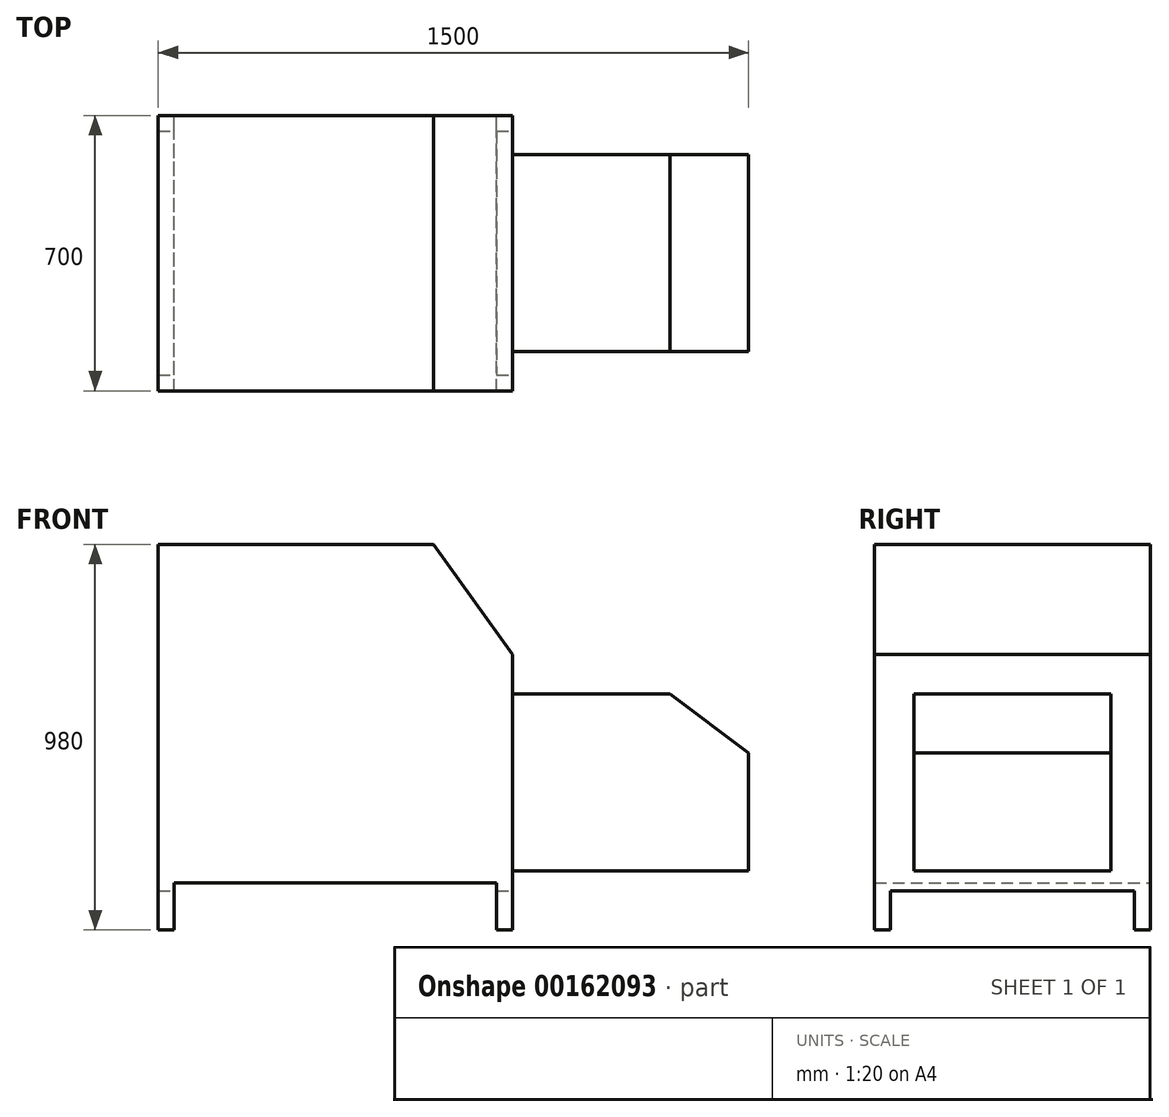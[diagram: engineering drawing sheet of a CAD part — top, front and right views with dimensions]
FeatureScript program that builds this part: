
annotation { "Feature Type Name" : "Feature", "Feature Type Description" : "" }
export const myFeature = defineFeature(function(context is Context, id is Id, definition is map)
    precondition{}
    {
        {
            var Q0;
            Q0=qCreatedBy(makeId("Front.planeOp"),FACE);
            var sketch = newSketch(context, id + "F0", { "sketchPlane" : qUnion([Q0])});
            skLineSegment(sketch, "E0", {"start": v(0, 0) * mm, "end": v(0, 980) * mm});
            skLineSegment(sketch, "E1", {"start": v(0, 980) * mm, "end": v(700, 980) * mm});
            skLineSegment(sketch, "E2", {"start": v(700, 980) * mm, "end": v(900, 700) * mm});
            skLineSegment(sketch, "E3", {"start": v(900, 700) * mm, "end": v(900, 0) * mm});
            skLineSegment(sketch, "E4", {"start": v(900, 0) * mm, "end": v(860, 0) * mm});
            skLineSegment(sketch, "E5", {"start": v(860, 0) * mm, "end": v(860, 120) * mm});
            skLineSegment(sketch, "E6", {"start": v(860, 120) * mm, "end": v(40, 120) * mm});
            skLineSegment(sketch, "E7", {"start": v(40, 120) * mm, "end": v(40, 0) * mm});
            skLineSegment(sketch, "E8", {"start": v(40, 0) * mm, "end": v(0, 0) * mm});
            skSolve(sketch);
        }
        {
            var Q0;
            Q0 = qSketchRegion(id + "F0", true);
            extrude(context, id + "F1", {"entities" : qUnion([Q0]), "depth" : 700 * mm});
        }
        {
            var Q0;
            Q0=makeQuery(id+"F1.opExtrude","SWEPT_FACE",FACE,{"disambiguationData":[OSD([sQuery(id+"F0.wireOp",EDGE,"E3")])]});
            var sketch = newSketch(context, id + "F2", { "sketchPlane" : qUnion([Q0])});
            skLineSegment(sketch, "E9.bottom", {"start": v(-600, 600) * mm, "end": v(-100, 600) * mm});
            skLineSegment(sketch, "E9.top", {"start": v(-600, 150) * mm, "end": v(-100, 150) * mm});
            skLineSegment(sketch, "E9.left", {"start": v(-600, 600) * mm, "end": v(-600, 150) * mm});
            skLineSegment(sketch, "E9.right", {"start": v(-100, 600) * mm, "end": v(-100, 150) * mm});
            skSolve(sketch);
        }
        {
            var Q0;
            Q0 = qSketchRegion(id + "F2", true);
            extrude(context, id + "F3", {"entities" : qUnion([Q0]), "operationType" : NewBodyOperationType.ADD, "depth" : 600 * mm});
        }
        {
            var Q0;
            Q0=makeQuery(id+"F3.opExtrude","SWEPT_FACE",FACE,{"disambiguationData":[OSD([sQuery(id+"F2.wireOp",EDGE,"E9.left")])]});
            var sketch = newSketch(context, id + "F4", { "sketchPlane" : qUnion([Q0])});
            skLineSegment(sketch, "E10", {"start": v(1500, 600) * mm, "end": v(1300, 600) * mm});
            skLineSegment(sketch, "E11", {"start": v(1300, 600) * mm, "end": v(1500, 450) * mm});
            skLineSegment(sketch, "E12", {"start": v(1500, 450) * mm, "end": v(1500, 600) * mm});
            skSolve(sketch);
        }
        {
            var Q0;
            Q0 = qSketchRegion(id + "F4", true);
            extrude(context, id + "F5", {"entities" : qUnion([Q0]), "operationType" : NewBodyOperationType.REMOVE, "endBound" : BoundingType.THROUGH_ALL, "oppositeDirection" : true, "depth" : 25 * mm});
        }
        {
            var Q0;
            Q0=makeQuery(id+"F1.opExtrude","SWEPT_FACE",FACE,{"disambiguationData":[OSD([sQuery(id+"F0.wireOp",EDGE,"E3")])]});
            var sketch = newSketch(context, id + "F6", { "sketchPlane" : qUnion([Q0])});
            skLineSegment(sketch, "E13.bottom", {"start": v(-660, 0) * mm, "end": v(-40, 0) * mm});
            skLineSegment(sketch, "E13.top", {"start": v(-660, 100) * mm, "end": v(-40, 100) * mm});
            skLineSegment(sketch, "E13.left", {"start": v(-660, 0) * mm, "end": v(-660, 100) * mm});
            skLineSegment(sketch, "E13.right", {"start": v(-40, 0) * mm, "end": v(-40, 100) * mm});
            skSolve(sketch);
        }
        {
            var Q0;
            Q0 = qSketchRegion(id + "F6", true);
            extrude(context, id + "F7", {"entities" : qUnion([Q0]), "operationType" : NewBodyOperationType.REMOVE, "endBound" : BoundingType.THROUGH_ALL, "oppositeDirection" : true, "depth" : 25 * mm});
        }
    });
